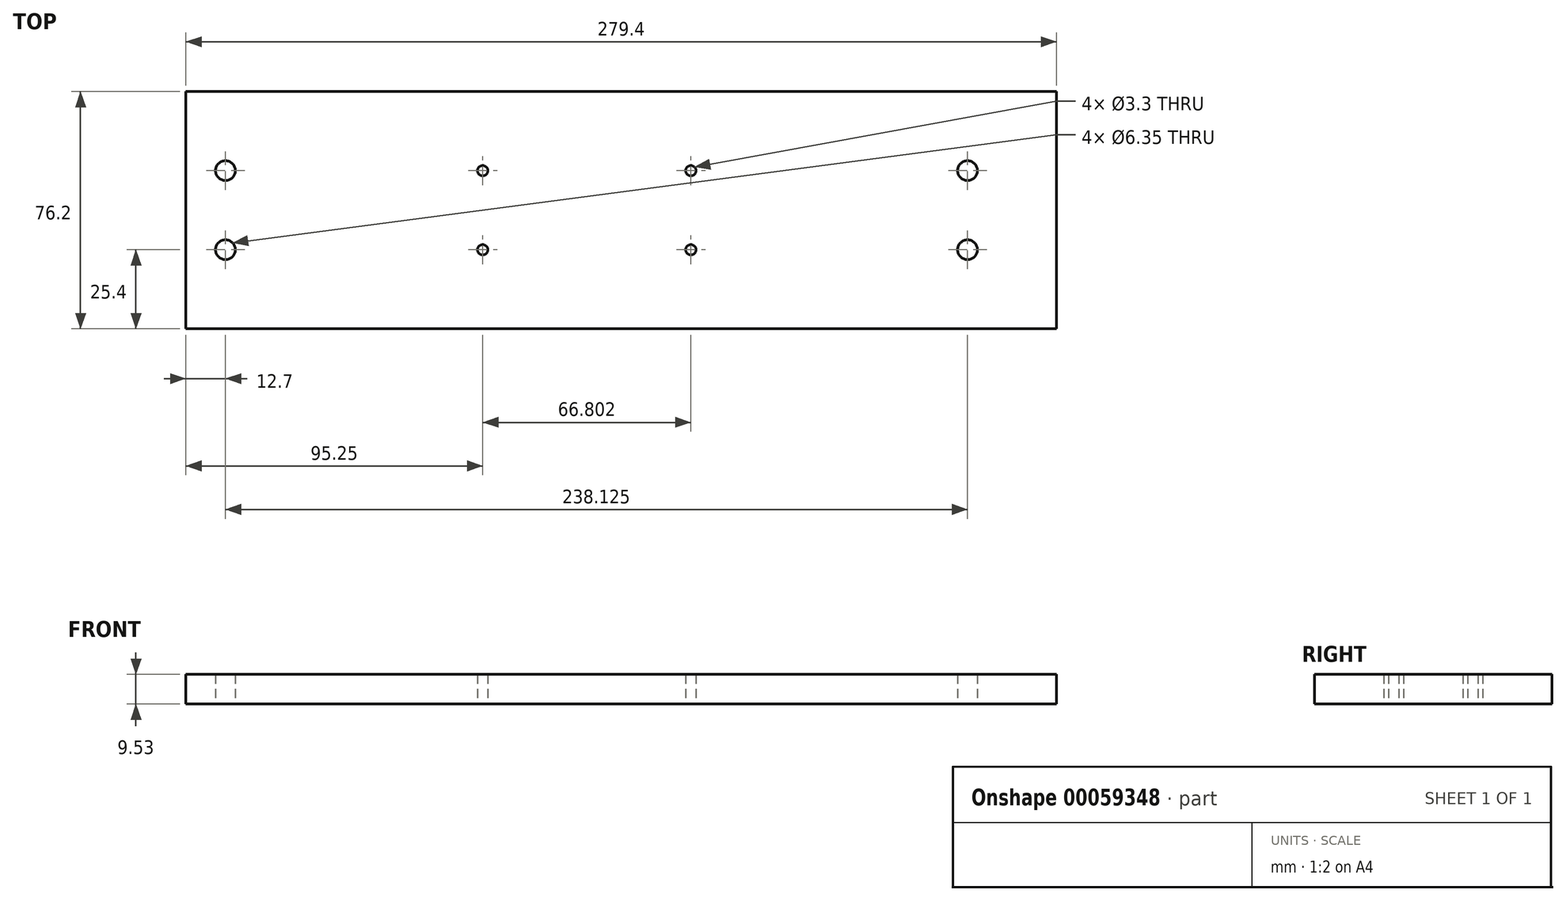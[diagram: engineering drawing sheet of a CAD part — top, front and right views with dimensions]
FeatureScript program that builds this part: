
annotation { "Feature Type Name" : "Feature", "Feature Type Description" : "" }
export const myFeature = defineFeature(function(context is Context, id is Id, definition is map)
    precondition{}
    {
        {
            var Q0;
            Q0=qCreatedBy(makeId("Top.planeOp"),FACE);
            var sketch = newSketch(context, id + "F0", { "sketchPlane" : qUnion([Q0])});
            skLineSegment(sketch, "E0.bottom", {"start": v(-152.4, 38.1) * mm, "end": v(127, 38.1) * mm});
            skLineSegment(sketch, "E0.top", {"start": v(-152.4, -38.1) * mm, "end": v(127, -38.1) * mm});
            skLineSegment(sketch, "E0.left", {"start": v(-152.4, 38.1) * mm, "end": v(-152.4, -38.1) * mm});
            skLineSegment(sketch, "E0.right", {"start": v(127, 38.1) * mm, "end": v(127, -38.1) * mm});
            skLineSegment(sketch, "E1", {"start": v(0, 0) * mm, "end": v(-197.6, 0) * mm});
            skLineSegment(sketch, "E2", {"start": v(0, 0) * mm, "end": v(0, 96.89) * mm});
            skCircle(sketch, "E3", {"center": v(-139.7, 12.7) * mm, "radius": 3.18 * mm});
            skCircle(sketch, "E4", {"center": v(-139.7, -12.7) * mm, "radius": 3.18 * mm});
            skCircle(sketch, "E5", {"center": v(-57.15, 12.7) * mm, "radius": 1.65 * mm});
            skCircle(sketch, "E6", {"center": v(-57.15, -12.7) * mm, "radius": 1.65 * mm});
            skCircle(sketch, "E7", {"center": v(9.65, 12.7) * mm, "radius": 1.65 * mm});
            skCircle(sketch, "E8", {"center": v(9.65, -12.7) * mm, "radius": 1.65 * mm});
            skCircle(sketch, "E9", {"center": v(98.42, 12.7) * mm, "radius": 3.18 * mm});
            skCircle(sketch, "E10", {"center": v(98.42, -12.7) * mm, "radius": 3.18 * mm});
            skSolve(sketch);
        }
        {
            var Q0;
            Q0=makeQuery(id+"F0.imprint","IMPRINT",FACE,{"disambiguationData":[TD([[makeQuery(id+"F0.imprint","IMPRINT",EDGE,{"derivedFrom":sQuery(id+"F0.wireOp",EDGE,"E3")}),-1.0]])]});
            var Q1;
            {var subQ8=sQuery(id+"F0.wireOp",EDGE,"E0.top");Q1=makeQuery(id+"F0.imprint","IMPRINT",FACE,{"disambiguationData":[TD([[makeQuery(id+"F0.imprint","IMPRINT",EDGE,{"derivedFrom":subQ8}),1.0]])]});}
            extrude(context, id + "F1", {"entities" : qUnion([Q0, Q1]), "depth" : 9.52 * mm});
        }
    });
